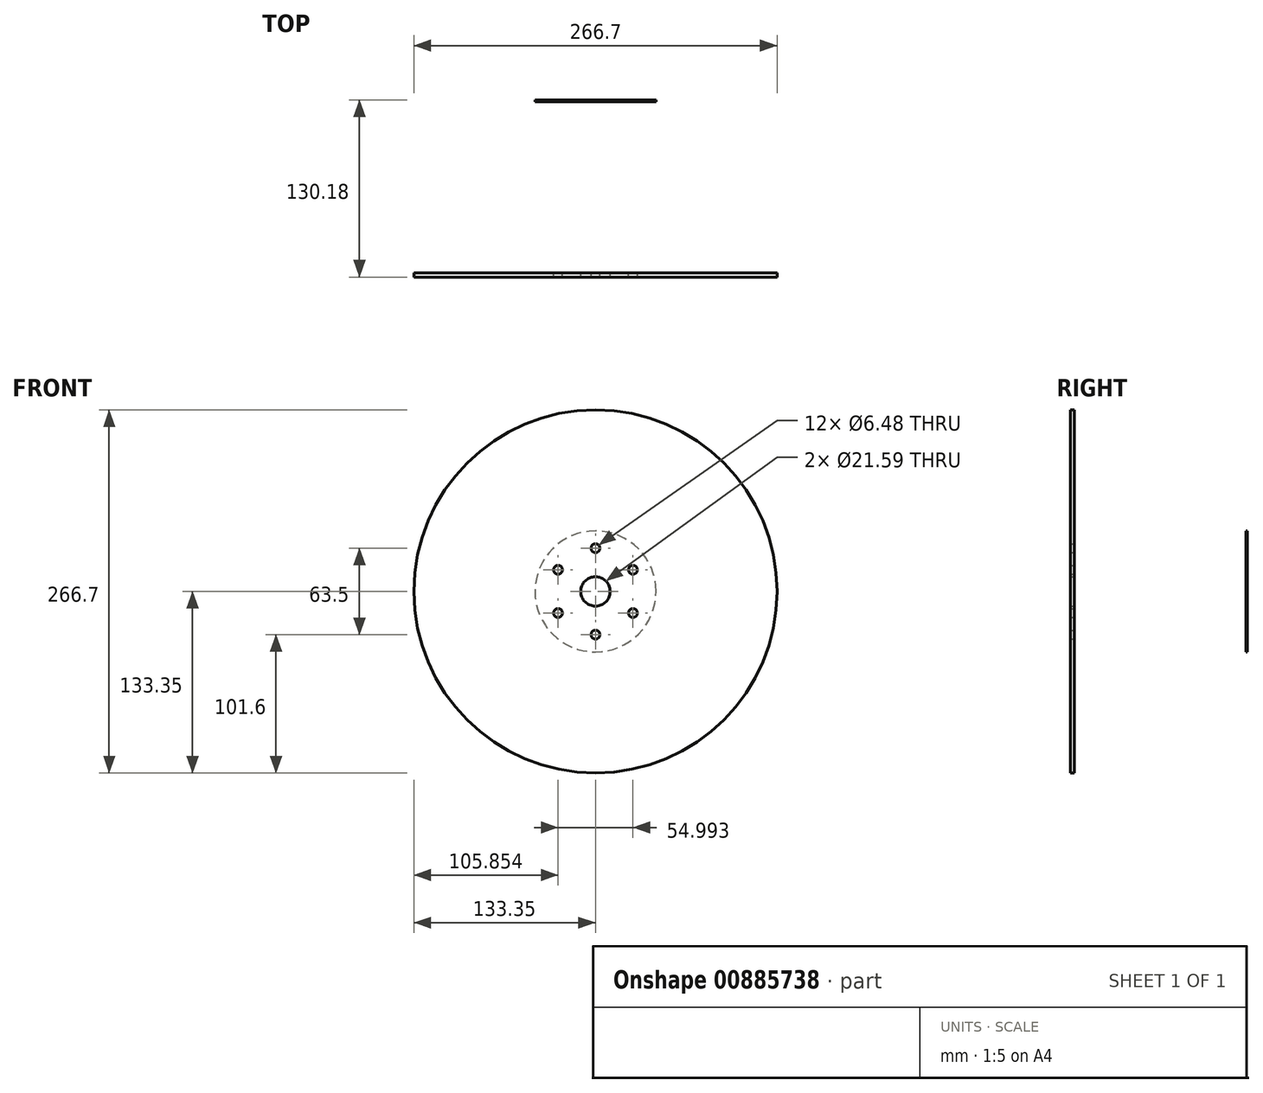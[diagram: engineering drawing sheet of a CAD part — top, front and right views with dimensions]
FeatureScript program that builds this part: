
annotation { "Feature Type Name" : "Feature", "Feature Type Description" : "" }
export const myFeature = defineFeature(function(context is Context, id is Id, definition is map)
    precondition{}
    {
        {
            var Q0;
            Q0=qCreatedBy(makeId("Front.planeOp"),FACE);
            var sketch = newSketch(context, id + "F0", { "sketchPlane" : qUnion([Q0])});
            skCircle(sketch, "E0", {"center": v(0, 0) * mm, "radius": 44.45 * mm});
            skCircle(sketch, "E1", {"center": v(0, 0) * mm, "radius": 10.8 * mm});
            skLineSegment(sketch, "E2", {"start": v(0, 44.45) * mm, "end": v(0, -44.45) * mm, "construction": true});
            skLineSegment(sketch, "E3", {"start": v(-44.45, 0) * mm, "end": v(44.45, 0) * mm, "construction": true});
            skCircle(sketch, "E4", {"center": v(0, 31.75) * mm, "radius": 3.24 * mm});
            skCircle(sketch, "E5.1.0", {"center": v(-27.5, 15.88) * mm, "radius": 3.24 * mm});
            skCircle(sketch, "E5.2.0", {"center": v(-27.5, -15.87) * mm, "radius": 3.24 * mm});
            skCircle(sketch, "E5.3.0", {"center": v(0, -31.75) * mm, "radius": 3.24 * mm});
            skCircle(sketch, "E5.4.0", {"center": v(27.5, -15.88) * mm, "radius": 3.24 * mm});
            skCircle(sketch, "E5.5.0", {"center": v(27.5, 15.88) * mm, "radius": 3.24 * mm});
            skSolve(sketch);
        }
        {
            var Q0;
            Q0 = qSketchRegion(id + "F0", true);
            extrude(context, id + "F1", {"entities" : qUnion([Q0]), "depth" : 1.27 * mm, "offsetDistance" : 25.4 * mm});
        }
        {
            var Q0;
            Q0=qCreatedBy(makeId("Front.planeOp"),FACE);
            cPlane(context, id + "F2", {"entities" : qUnion([Q0]), "cplaneType" : CPlaneType.OFFSET, "offset" : 127 * mm, "width" : 152.4 * mm, "height" : 152.4 * mm});
        }
        {
            var Q0;
            Q0=qCreatedBy(id+"F2.planeOp",FACE);
            var sketch = newSketch(context, id + "F3", { "sketchPlane" : qUnion([Q0])});
            skCircle(sketch, "E6.0", {"center": v(0, 31.75) * mm, "radius": 3.24 * mm});
            skCircle(sketch, "E7.0", {"center": v(27.5, 15.88) * mm, "radius": 3.24 * mm});
            skCircle(sketch, "E8.0", {"center": v(27.5, -15.88) * mm, "radius": 3.24 * mm});
            skCircle(sketch, "E9.0", {"center": v(0, -31.75) * mm, "radius": 3.24 * mm});
            skCircle(sketch, "E10.0", {"center": v(-27.5, -15.87) * mm, "radius": 3.24 * mm});
            skCircle(sketch, "E11.0", {"center": v(-27.5, 15.88) * mm, "radius": 3.24 * mm});
            skCircle(sketch, "E12.0", {"center": v(0, 0) * mm, "radius": 10.8 * mm});
            skCircle(sketch, "E13", {"center": v(0, 0) * mm, "radius": 133.35 * mm});
            skSolve(sketch);
        }
        {
            var Q0;
            Q0 = qSketchRegion(id + "F3", true);
            extrude(context, id + "F4", {"entities" : qUnion([Q0]), "depth" : 3.17 * mm, "offsetDistance" : 25.4 * mm});
        }
    });
